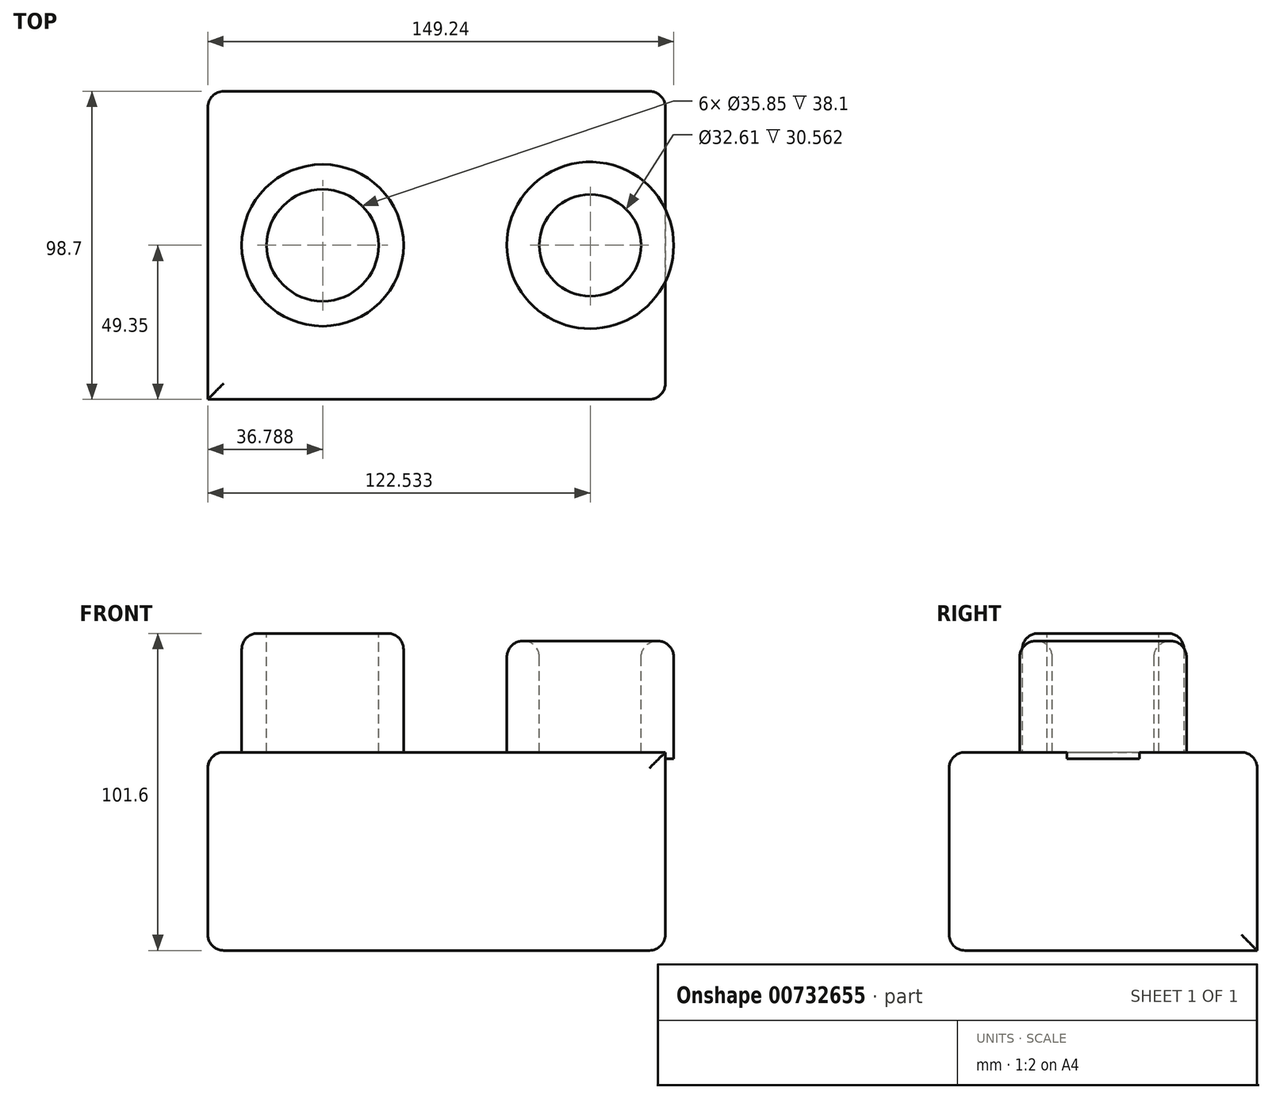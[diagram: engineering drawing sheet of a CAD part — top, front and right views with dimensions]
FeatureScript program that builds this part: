
annotation { "Feature Type Name" : "Feature", "Feature Type Description" : "" }
export const myFeature = defineFeature(function(context is Context, id is Id, definition is map)
    precondition{}
    {
        {
            var Q0;
            Q0=qCreatedBy(makeId("Top.planeOp"),FACE);
            var sketch = newSketch(context, id + "F0", { "sketchPlane" : qUnion([Q0])});
            skLineSegment(sketch, "E0.bottom", {"start": v(73.3, 49.35) * mm, "end": v(-73.3, 49.35) * mm});
            skLineSegment(sketch, "E0.top", {"start": v(73.3, -49.35) * mm, "end": v(-73.3, -49.35) * mm});
            skLineSegment(sketch, "E0.left", {"start": v(73.3, 49.35) * mm, "end": v(73.3, -49.35) * mm});
            skLineSegment(sketch, "E0.right", {"start": v(-73.3, 49.35) * mm, "end": v(-73.3, -49.35) * mm});
            skPoint(sketch, "E0.middle", {"position": v(0, 0) * mm});
            skSolve(sketch);
        }
        {
            var Q0;
            Q0=makeQuery(id+"F0.imprint","IMPRINT",FACE,{"disambiguationData":[TD([[makeQuery(id+"F0.imprint","IMPRINT",EDGE,{"derivedFrom":sQuery(id+"F0.wireOp",EDGE,"E0.bottom")}),1.0]])]});
            extrude(context, id + "F1", {"entities" : qUnion([Q0]), "depth" : 63.5 * mm, "offsetDistance" : 25.4 * mm});
        }
        {
            var Q0;
            Q0=makeQuery(id+"F1.opExtrude","CAP_FACE",FACE,{"disambiguationData":[OSD([sQuery(id+"F0.wireOp",EDGE,"E0.bottom"),sQuery(id+"F0.wireOp",EDGE,"E0.top"),sQuery(id+"F0.wireOp",EDGE,"E0.left"),sQuery(id+"F0.wireOp",EDGE,"E0.right")])],"isStart":false});
            var sketch = newSketch(context, id + "F2", { "sketchPlane" : qUnion([Q0])});
            skCircle(sketch, "E1", {"center": v(-36.5, 0) * mm, "radius": 25.91 * mm});
            skSolve(sketch);
        }
        {
            var Q0;
            Q0=makeQuery(id+"F2.imprint","IMPRINT",FACE,{"disambiguationData":[TD([[makeQuery(id+"F2.imprint","IMPRINT",EDGE,{"derivedFrom":sQuery(id+"F2.wireOp",EDGE,"E1")}),1.0]])]});
            extrude(context, id + "F3", {"entities" : qUnion([Q0]), "depth" : 38.1 * mm, "offsetDistance" : 25.4 * mm});
        }
        {
            var Q0;
            Q0=makeQuery(id+"F3.opExtrude","CAP_FACE",FACE,{"disambiguationData":[OSD([sQuery(id+"F2.wireOp",EDGE,"E1")])],"isStart":false});
            var sketch = newSketch(context, id + "F4", { "sketchPlane" : qUnion([Q0])});
            skCircle(sketch, "E2", {"center": v(-36.5, 0) * mm, "radius": 17.92 * mm});
            skSolve(sketch);
        }
        {
            var Q0;
            Q0=makeQuery(id+"F4.imprint","IMPRINT",FACE,{"disambiguationData":[TD([[makeQuery(id+"F4.imprint","IMPRINT",EDGE,{"derivedFrom":sQuery(id+"F4.wireOp",EDGE,"E2")}),1.0]])]});
            var Q1;
            Q1=makeQuery(id+"F1.opExtrude","CAP_FACE",FACE,{"disambiguationData":[OSD([sQuery(id+"F0.wireOp",EDGE,"E0.bottom"),sQuery(id+"F0.wireOp",EDGE,"E0.top"),sQuery(id+"F0.wireOp",EDGE,"E0.left"),sQuery(id+"F0.wireOp",EDGE,"E0.right")])],"isStart":false});
            extrude(context, id + "F5", {"entities" : qUnion([Q0]), "operationType" : NewBodyOperationType.REMOVE, "endBound" : BoundingType.UP_TO_SURFACE, "oppositeDirection" : true, "depth" : 25.4 * mm, "endBoundEntityFace" : qUnion([Q1]), "offsetDistance" : 25.4 * mm});
        }
        {
            var Q0;
            Q0=qCreatedBy(makeId("Front.planeOp"),FACE);
            var sketch = newSketch(context, id + "F6", { "sketchPlane" : qUnion([Q0])});
            skLineSegment(sketch, "E3", {"start": v(49.24, 92.59) * mm, "end": v(49.24, 34.09) * mm});
            skLineSegment(sketch, "E4.bottom", {"start": v(22.53, 99.14) * mm, "end": v(32.94, 99.14) * mm});
            skLineSegment(sketch, "E4.top", {"start": v(22.53, 61.46) * mm, "end": v(32.94, 61.46) * mm});
            skLineSegment(sketch, "E4.left", {"start": v(22.53, 99.14) * mm, "end": v(22.53, 61.46) * mm});
            skLineSegment(sketch, "E4.right", {"start": v(32.94, 99.14) * mm, "end": v(32.94, 61.46) * mm});
            skSolve(sketch);
        }
        {
            var Q0;
            Q0=makeQuery(id+"F6.imprint","IMPRINT",FACE,{"disambiguationData":[TD([[makeQuery(id+"F6.imprint","IMPRINT",EDGE,{"derivedFrom":sQuery(id+"F6.wireOp",EDGE,"E4.bottom")}),-1.0]])]});
            var Q1;
            Q1=sQuery(id+"F6.wireOp",EDGE,"E3");
            revolve(context, id + "F7", {"operationType" : NewBodyOperationType.ADD, "entities" : qUnion([Q0]), "axis" : qUnion([Q1]), "revolveType" : RevolveType.FULL});
        }
        {
            var Q0;
            Q0=makeQuery(id+"F7.opRevolve","SWEPT_EDGE",EDGE,{"disambiguationData":[OSD([sQuery(id+"F6.wireOp",EDGE,"E4.bottom"),sQuery(id+"F6.wireOp",EDGE,"E4.left")])]});
            var Q1;
            Q1=makeQuery(id+"F7.opRevolve","SWEPT_EDGE",EDGE,{"disambiguationData":[OSD([sQuery(id+"F6.wireOp",EDGE,"E4.bottom"),sQuery(id+"F6.wireOp",EDGE,"E4.right")])]});
            var Q2;
            Q2=makeQuery(id+"F3.opExtrude","CAP_EDGE",EDGE,{"disambiguationData":[OSD([sQuery(id+"F2.wireOp",EDGE,"E1")])],"isStart":false});
            var Q3;
            Q3=makeQuery(id+"F1.opExtrude","CAP_EDGE",EDGE,{"disambiguationData":[OSD([sQuery(id+"F0.wireOp",EDGE,"E0.top")])],"isStart":false});
            var Q4;
            Q4=makeQuery(id+"F1.opExtrude","SWEPT_EDGE",EDGE,{"disambiguationData":[OSD([sQuery(id+"F0.wireOp",EDGE,"E0.top"),sQuery(id+"F0.wireOp",EDGE,"E0.left")])]});
            var Q5;
            Q5=makeQuery(id+"F1.opExtrude","CAP_EDGE",EDGE,{"disambiguationData":[OSD([sQuery(id+"F0.wireOp",EDGE,"E0.top")])],"isStart":true});
            var Q6;
            Q6=makeQuery(id+"F1.opExtrude","SWEPT_EDGE",EDGE,{"disambiguationData":[OSD([sQuery(id+"F0.wireOp",EDGE,"E0.bottom"),sQuery(id+"F0.wireOp",EDGE,"E0.left")])]});
            var Q7;
            Q7=makeQuery(id+"F1.opExtrude","CAP_EDGE",EDGE,{"disambiguationData":[OSD([sQuery(id+"F0.wireOp",EDGE,"E0.left")])],"isStart":true});
            var Q8;
            Q8=makeQuery(id+"F1.opExtrude","CAP_EDGE",EDGE,{"disambiguationData":[OSD([sQuery(id+"F0.wireOp",EDGE,"E0.right")])],"isStart":false});
            var Q9;
            Q9=makeQuery(id+"F1.opExtrude","SWEPT_EDGE",EDGE,{"disambiguationData":[OSD([sQuery(id+"F0.wireOp",EDGE,"E0.bottom"),sQuery(id+"F0.wireOp",EDGE,"E0.right")])]});
            var Q10;
            Q10=makeQuery(id+"F1.opExtrude","CAP_EDGE",EDGE,{"disambiguationData":[OSD([sQuery(id+"F0.wireOp",EDGE,"E0.bottom")])],"isStart":false});
            var Q11;
            Q11=makeQuery(id+"F1.opExtrude","CAP_EDGE",EDGE,{"disambiguationData":[OSD([sQuery(id+"F0.wireOp",EDGE,"E0.right")])],"isStart":true});
            fillet(context, id + "F8", {"entities" : qUnion([Q0, Q1, Q2, Q3, Q4, Q5, Q6, Q7, Q8, Q9, Q10, Q11]), "radius" : 5.08 * mm, "tangentPropagation" : true, "allowEdgeOverflow" : false});
        }
    });
